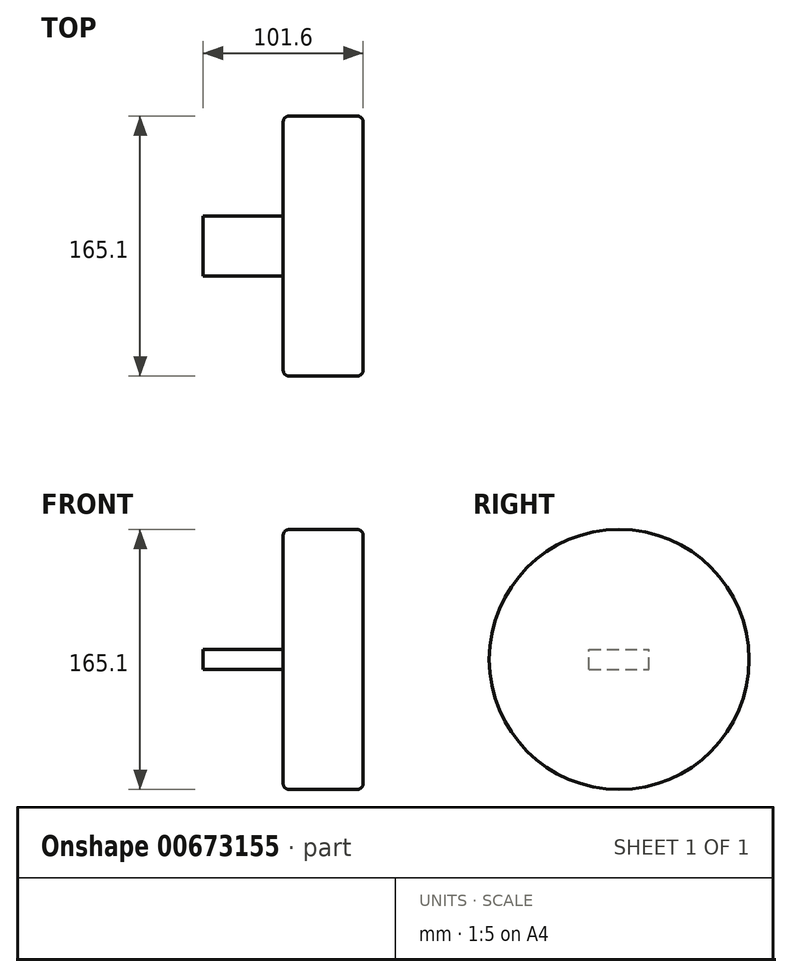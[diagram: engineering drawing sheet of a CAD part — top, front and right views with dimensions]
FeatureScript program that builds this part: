
annotation { "Feature Type Name" : "Feature", "Feature Type Description" : "" }
export const myFeature = defineFeature(function(context is Context, id is Id, definition is map)
    precondition{}
    {
        {
            var Q0;
            Q0=qCreatedBy(makeId("Right.planeOp"),FACE);
            var sketch = newSketch(context, id + "F0", { "sketchPlane" : qUnion([Q0])});
            skCircle(sketch, "E0", {"center": v(0, 0) * mm, "radius": 82.55 * mm});
            skSolve(sketch);
        }
        {
            var Q0;
            Q0 = qSketchRegion(id + "F0", true);
            extrude(context, id + "F1", {"entities" : qUnion([Q0]), "depth" : 50.8 * mm, "offsetDistance" : 25.4 * mm});
        }
        {
            var Q0;
            Q0=makeQuery(id+"F1.opExtrude","CAP_EDGE",EDGE,{"disambiguationData":[OSD([sQuery(id+"F0.wireOp",EDGE,"E0")])],"isStart":false});
            var Q1;
            Q1=makeQuery(id+"F1.opExtrude","CAP_EDGE",EDGE,{"disambiguationData":[OSD([sQuery(id+"F0.wireOp",EDGE,"E0")])],"isStart":true});
            fillet(context, id + "F2", {"entities" : qUnion([Q0, Q1]), "radius" : 3.8 * mm, "tangentPropagation" : true, "allowEdgeOverflow" : false});
        }
        {
            var Q0;
            Q0=makeQuery(id+"F1.opExtrude","CAP_FACE",FACE,{"disambiguationData":[OSD([sQuery(id+"F0.wireOp",EDGE,"E0")])],"isStart":true});
            var sketch = newSketch(context, id + "F3", { "sketchPlane" : qUnion([Q0])});
            skLineSegment(sketch, "E1.bottom", {"start": v(19.05, -6.35) * mm, "end": v(-19.05, -6.35) * mm});
            skLineSegment(sketch, "E1.top", {"start": v(19.05, 6.35) * mm, "end": v(-19.05, 6.35) * mm});
            skLineSegment(sketch, "E1.left", {"start": v(19.05, -6.35) * mm, "end": v(19.05, 6.35) * mm});
            skLineSegment(sketch, "E1.right", {"start": v(-19.05, -6.35) * mm, "end": v(-19.05, 6.35) * mm});
            skPoint(sketch, "E1.middle", {"position": v(0, 0) * mm});
            skSolve(sketch);
        }
        {
            var Q0;
            Q0=makeQuery(id+"F3.imprint","IMPRINT",FACE,{"disambiguationData":[TD([[makeQuery(id+"F3.imprint","IMPRINT",EDGE,{"derivedFrom":sQuery(id+"F3.wireOp",EDGE,"E1.bottom")}),-1.0]])]});
            extrude(context, id + "F4", {"entities" : qUnion([Q0]), "operationType" : NewBodyOperationType.ADD, "depth" : 50.8 * mm, "offsetDistance" : 25.4 * mm});
        }
    });
